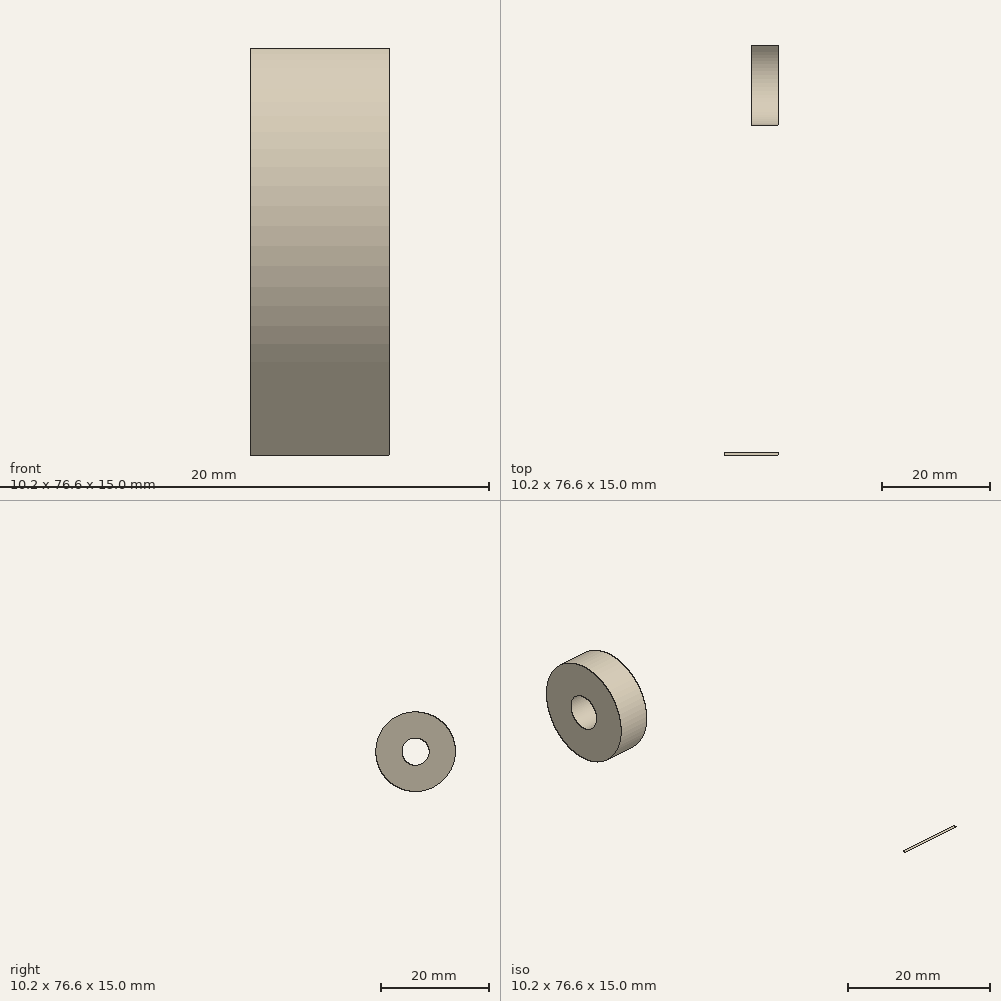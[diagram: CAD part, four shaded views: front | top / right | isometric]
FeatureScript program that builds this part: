
annotation { "Feature Type Name" : "Feature", "Feature Type Description" : "" }
export const myFeature = defineFeature(function(context is Context, id is Id, definition is map)
    precondition{}
    {
        {
            var Q0;
            Q0=qCreatedBy(makeId("Right.planeOp"),FACE);
            var sketch = newSketch(context, id + "F0", { "sketchPlane" : qUnion([Q0])});
            skCircle(sketch, "E0", {"center": v(-68.94, 0) * mm, "radius": 7.54 * mm});
            skCircle(sketch, "E1", {"center": v(0, 0) * mm, "radius": 7.45 * mm});
            skLineSegment(sketch, "E2", {"start": v(-69.17, 7.53) * mm, "end": v(-7.45, 7.46) * mm});
            skLineSegment(sketch, "E3", {"start": v(-69.18, -7.53) * mm, "end": v(0, -7.45) * mm});
            skLineSegment(sketch, "E4", {"start": v(-7.45, 0) * mm, "end": v(-7.45, 7.46) * mm});
            skPoint(sketch, "E5.orphan", {"position": v(0, 7.45) * mm});
            skSolve(sketch);
        }
        {
            var Q0;
            {var subQ0=sQuery(id+"F0.wireOp",EDGE,"E2");var subQ1=sQuery(id+"F0.wireOp",EDGE,"E0");var subQ2=makeQuery(id+"F0.imprint","INTERSECT",VERTEX,{"disambiguationData":[OD(0.0)],"derivedFrom":[subQ1,subQ0]});Q0=makeQuery(id+"F0.imprint","IMPRINT",FACE,{"disambiguationData":[TD([[makeQuery(id+"F0.imprint","IMPRINT",EDGE,{"disambiguationData":[TD([[subQ2,-1.0]])],"derivedFrom":subQ1}),1.0]])]});}
            var Q1;
            {var subQ0=sQuery(id+"F0.wireOp",EDGE,"E2");var subQ1=sQuery(id+"F0.wireOp",EDGE,"E0");var subQ2=makeQuery(id+"F0.imprint","INTERSECT",VERTEX,{"disambiguationData":[OD(1.0)],"derivedFrom":[subQ1,subQ0]});Q1=makeQuery(id+"F0.imprint","IMPRINT",FACE,{"disambiguationData":[TD([[makeQuery(id+"F0.imprint","IMPRINT",EDGE,{"disambiguationData":[TD([[subQ2,1.0]])],"derivedFrom":subQ1}),-1.0]])]});}
            extrude(context, id + "F1", {"entities" : qUnion([Q0, Q1]), "depth" : 5.08 * mm, "offsetDistance" : 25.4 * mm, "hasSecondDirection" : true, "secondDirectionOppositeDirection" : true, "secondDirectionDepth" : 5.08 * mm});
        }
        {
            var Q0;
            {var subQ0=sQuery(id+"F0.wireOp",EDGE,"E1");var subQ1=makeQuery(id+"F0.imprint","INTERSECT",VERTEX,{"derivedFrom":[subQ0,sQuery(id+"F0.wireOp",EDGE,"E2")]});Q0=makeQuery(id+"F0.imprint","IMPRINT",FACE,{"disambiguationData":[TD([[makeQuery(id+"F0.imprint","IMPRINT",EDGE,{"disambiguationData":[TD([[subQ1,-1.0]])],"derivedFrom":subQ0}),1.0]])]});}
            extrude(context, id + "F2", {"entities" : qUnion([Q0]), "depth" : 5.08 * mm, "offsetDistance" : 25.4 * mm});
        }
        {
            var Q0;
            Q0=sQuery(id+"F0.wireOp",VERTEX,"E1.center");
            var Q1;
            Q1=makeQuery(id+"F2.opExtrude","SWEPT_BODY",BODY,{"disambiguationData":[OSD([sQuery(id+"F0.wireOp",EDGE,"E1")])]});
            hole(context, id + "F3", {"style" : HoleStyle.SIMPLE, "endStyle" : HoleEndStyle.BLIND, "oppositeDirection" : true, "holeDiameter" : 5.08 * mm, "majorDiameter" : 6.35 * mm, "holeDepth" : 10.16 * mm, "isTappedThrough" : true, "tappedDepth" : 12.7 * mm, "tapClearance" : 3, "locations" : qUnion([Q0]), "scope" : qUnion([Q1])});
        }
        {
            var Q0;
            Q0=sQuery(id+"F0.wireOp",VERTEX,"E0.center");
            var Q1;
            Q1=makeQuery(id+"F1.opExtrude","SWEPT_BODY",BODY,{"disambiguationData":[OSD([sQuery(id+"F0.wireOp",EDGE,"E0"),sQuery(id+"F0.wireOp",EDGE,"E1"),sQuery(id+"F0.wireOp",EDGE,"E2"),sQuery(id+"F0.wireOp",EDGE,"E3"),sQuery(id+"F0.wireOp",EDGE,"E4")])]});
            hole(context, id + "F4", {"style" : HoleStyle.SIMPLE, "endStyle" : HoleEndStyle.BLIND, "oppositeDirection" : true, "holeDiameter" : 10.16 * mm, "majorDiameter" : 6.35 * mm, "holeDepth" : 10.16 * mm, "isTappedThrough" : true, "tappedDepth" : 12.7 * mm, "tapClearance" : 3, "locations" : qUnion([Q0]), "scope" : qUnion([Q1])});
        }
        {
            var Q0;
            Q0=sQuery(id+"F0.wireOp",VERTEX,"E0.center");
            var Q1;
            Q1=makeQuery(id+"F1.opExtrude","SWEPT_BODY",BODY,{"disambiguationData":[OSD([sQuery(id+"F0.wireOp",EDGE,"E0"),sQuery(id+"F0.wireOp",EDGE,"E1"),sQuery(id+"F0.wireOp",EDGE,"E2"),sQuery(id+"F0.wireOp",EDGE,"E3"),sQuery(id+"F0.wireOp",EDGE,"E4")])]});
            hole(context, id + "F5", {"style" : HoleStyle.SIMPLE, "endStyle" : HoleEndStyle.BLIND, "holeDiameter" : 10.16 * mm, "majorDiameter" : 6.35 * mm, "holeDepth" : 10.16 * mm, "isTappedThrough" : true, "tappedDepth" : 12.7 * mm, "tapClearance" : 3, "locations" : qUnion([Q0]), "scope" : qUnion([Q1])});
        }
        {
            var Q0;
            Q0=sQuery(id+"F0.wireOp",VERTEX,"E1.center");
            var Q1;
            Q1=makeQuery(id+"F2.opExtrude","SWEPT_BODY",BODY,{"disambiguationData":[OSD([sQuery(id+"F0.wireOp",EDGE,"E1")])]});
            hole(context, id + "F6", {"style" : HoleStyle.SIMPLE, "endStyle" : HoleEndStyle.BLIND, "holeDiameter" : 5.08 * mm, "majorDiameter" : 6.35 * mm, "holeDepth" : 10.16 * mm, "isTappedThrough" : true, "tappedDepth" : 12.7 * mm, "tapClearance" : 3, "locations" : qUnion([Q0]), "scope" : qUnion([Q1])});
        }
    });
